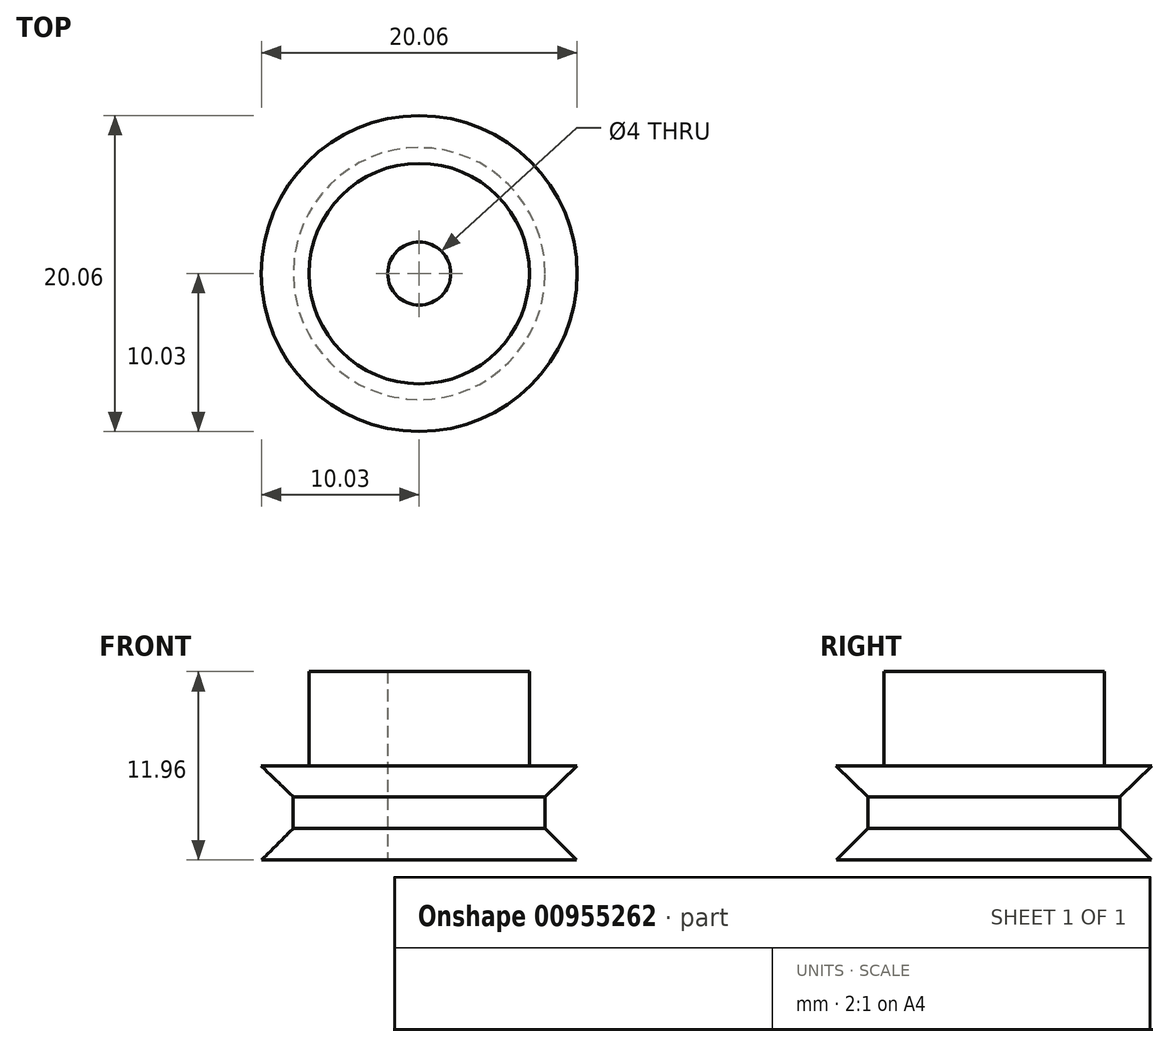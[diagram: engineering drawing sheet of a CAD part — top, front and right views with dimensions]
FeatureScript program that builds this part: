
annotation { "Feature Type Name" : "Feature", "Feature Type Description" : "" }
export const myFeature = defineFeature(function(context is Context, id is Id, definition is map)
    precondition{}
    {
        {
            var Q0;
            Q0=qCreatedBy(makeId("Front.planeOp"),FACE);
            var sketch = newSketch(context, id + "F0", { "sketchPlane" : qUnion([Q0])});
            skLineSegment(sketch, "E0", {"start": v(0, 0) * mm, "end": v(0, 5.96) * mm});
            skLineSegment(sketch, "E1", {"start": v(7, 5.96) * mm, "end": v(10.03, 5.96) * mm});
            skLineSegment(sketch, "E2", {"start": v(10.03, 5.96) * mm, "end": v(8, 4) * mm});
            skLineSegment(sketch, "E3", {"start": v(8, 4) * mm, "end": v(8, 2) * mm});
            skLineSegment(sketch, "E4", {"start": v(8, 2) * mm, "end": v(10, 0) * mm});
            skLineSegment(sketch, "E5", {"start": v(10, 0) * mm, "end": v(0, 0) * mm});
            skLineSegment(sketch, "E6", {"start": v(0, 5.96) * mm, "end": v(0, 11.96) * mm});
            skLineSegment(sketch, "E7", {"start": v(0, 11.96) * mm, "end": v(7, 11.96) * mm});
            skLineSegment(sketch, "E8", {"start": v(7, 11.96) * mm, "end": v(7, 5.96) * mm});
            skLineSegment(sketch, "E9", {"start": v(2, 0) * mm, "end": v(2, 11.96) * mm});
            skPoint(sketch, "E9.endSnap0", {"position": v(3.5, 11.96) * mm});
            skSolve(sketch);
        }
        {
            var Q0;
            {var subQ0=sQuery(id+"F0.wireOp",EDGE,"E2");Q0=makeQuery(id+"F0.imprint","IMPRINT",FACE,{"disambiguationData":[TD([[makeQuery(id+"F0.imprint","IMPRINT",EDGE,{"derivedFrom":subQ0}),-1.0]])]});}
            var Q1;
            Q1=sQuery(id+"F0.wireOp",EDGE,"E0");
            revolve(context, id + "F1", {"surfaceOperationType" : NewSurfaceOperationType.NEW, "entities" : qUnion([Q0]), "axis" : qUnion([Q1]), "revolveType" : RevolveType.FULL});
        }
    });
